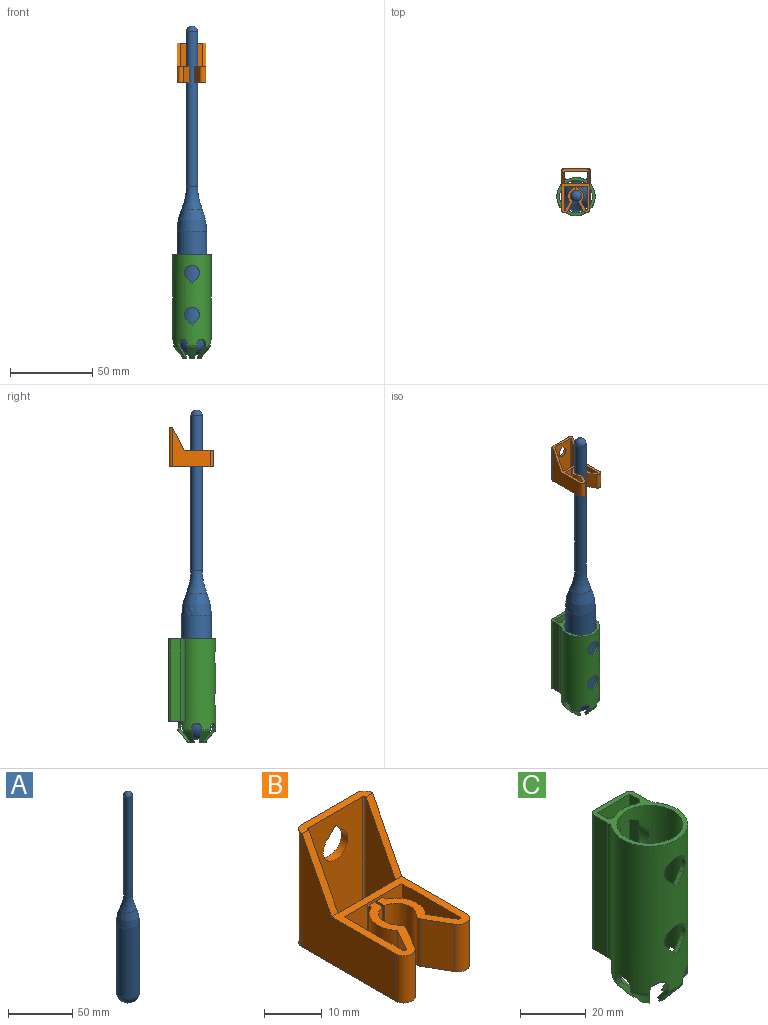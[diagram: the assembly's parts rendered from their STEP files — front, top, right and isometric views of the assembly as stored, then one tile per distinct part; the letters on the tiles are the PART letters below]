
ASSEMBLY  parts=3 mates=2
PART A: 6 faces, bbox 29.1x29.1x200 mm
  f0: cylinder r=9.02mm len=66.27mm, axis (0,0,-1), area 3754.8mm2, adj f1,f5
  f1: revolved ~18.03x18.03mm, area 710.2mm2, adj f0,f2
  f2: torus R=37.97mm, axis (0,0,-1), area 383.7mm2, adj f1,f3
  f3: cylinder r=3.43mm len=94.06mm, axis (0,0,-1), area 2026.6mm2, adj f2,f4
  f4: sphere r=3.43mm, area 73.9mm2, adj f3
  f5: sphere r=9.02mm, area 510.9mm2, adj f0
PART B: 42 faces, bbox 17.2x26.8x24 mm
  f0: plane 24x13.2mm, normal (0,-1,0), area 286.6mm2, adj f5,f7,f13,f27,f39,f40,f41
  f1: plane 24x13.2mm, normal (0,1,0), area 286.6mm2, adj f5,f7,f20,f33,f39,f40,f41
  f2: plane 24x7.2mm, normal (1,0,0), area 122.4mm2, adj f7,f13,f36,f37
  f3: plane 14.03x10mm, normal (-1,0,0), area 140.3mm2, adj f7,f26,f35,f38
  f4: plane 24x22.83mm, normal (1,0,0), area 278.7mm2, adj f7,f32,f33,f34,f35
  f5: plane 17.2x2mm, normal (0,0,1), area 27.2mm2, adj f0,f1,f13,f20,f27,f33,f34,f36
  f6: plane 10x1.6mm, normal (0,1,0), area 16mm2, adj f7,f8,f14,f35
  f7: plane 26.83x17.2mm, normal (0,0,-1), area 186.2mm2, adj f0,f1,f2,f3,f4,f6,f8,f9
  f8: plane 10x0.81mm, normal (-1,0,0), area 8.1mm2, adj f6,f7,f9,f35
  f9: cylinder r=5.03mm len=10mm, axis (0,0,-1), area 95.7mm2, adj f7,f8,f10,f35
  f10: plane 10x4.9mm, normal (-0.87,0.5,0), area 56.6mm2, adj f7,f9,f12,f35
  f11: plane 14.03x10mm, normal (1,0,0), area 140.3mm2, adj f7,f12,f35,f38
  f12: cylinder r=0.4mm len=10mm, axis (0,0,1), area 10.5mm2, adj f7,f10,f11,f35
  f13: cylinder r=0.4mm len=24mm, axis (0,0,1), area 15.1mm2, adj f0,f2,f5,f7
  f14: plane 10x2mm, normal (1,0,0), area 20mm2, adj f6,f7,f15,f35
  f15: cylinder r=3.43mm len=10mm, axis (0,0,-1), area 78.5mm2, adj f7,f14,f16,f35
  f16: cylinder r=1mm len=10mm, axis (0,0,-1), area 13.7mm2, adj f7,f15,f17,f35
  f17: plane 10x5.3mm, normal (0.87,-0.5,0), area 61.2mm2, adj f7,f16,f19,f35
  f18: plane 24x22.83mm, normal (-1,0,0), area 278.7mm2, adj f7,f19,f20,f35,f36
  f19: cylinder r=2mm len=10mm, axis (0,0,1), area 52.4mm2, adj f7,f17,f18,f35
  f20: cylinder r=2mm len=24mm, axis (0,0,1), area 75.4mm2, adj f1,f5,f7,f18
  f21: plane 10x1.6mm, normal (0,1,0), area 16mm2, adj f7,f22,f28,f35
  f22: plane 10x0.81mm, normal (1,0,0), area 8.1mm2, adj f7,f21,f23,f35
  f23: cylinder r=5.03mm len=10mm, axis (0,0,-1), area 95.7mm2, adj f7,f22,f24,f35
  f24: plane 10x4.9mm, normal (0.87,0.5,0), area 56.6mm2, adj f7,f23,f26,f35
  f25: plane 24x7.2mm, normal (-1,0,0), area 122.4mm2, adj f7,f27,f34,f37
  f26: cylinder r=0.4mm len=10mm, axis (0,0,1), area 10.5mm2, adj f3,f7,f24,f35
  f27: cylinder r=0.4mm len=24mm, axis (0,0,1), area 15.1mm2, adj f0,f5,f7,f25
  f28: plane 10x2mm, normal (-1,0,0), area 20mm2, adj f7,f21,f29,f35
  f29: cylinder r=3.43mm len=10mm, axis (0,0,-1), area 78.5mm2, adj f7,f28,f30,f35
  f30: cylinder r=1mm len=10mm, axis (0,0,-1), area 13.7mm2, adj f7,f29,f31,f35
  f31: plane 10x5.3mm, normal (-0.87,-0.5,0), area 61.2mm2, adj f7,f30,f32,f35
  f32: cylinder r=2mm len=10mm, axis (0,0,1), area 52.4mm2, adj f4,f7,f31,f35
  f33: cylinder r=2mm len=24mm, axis (0,0,1), area 75.4mm2, adj f1,f4,f5,f7
  f34: plane 14x7.2mm, normal (0,-0.89,0.46), area 25.2mm2, adj f4,f5,f25,f35
  f35: plane 17.63x17.2mm, normal (0,0,1), area 136mm2, adj f3,f4,f6,f8,f9,f10,f11,f12
  f36: plane 14x7.2mm, normal (0,-0.89,0.46), area 25.2mm2, adj f2,f5,f18,f35
  f37: plane 14x10mm, normal (0,1,0), area 140mm2, adj f2,f7,f25,f35
  f38: plane 14x10mm, normal (0,-1,0), area 140mm2, adj f3,f7,f11,f35
  f39: plane 2.12x2.12mm, normal (-0.71,0,-0.71), area 4.8mm2, adj f0,f1,f40,f41
  f40: plane 2.12x2.12mm, normal (0.71,0,-0.71), area 4.8mm2, adj f0,f1,f39,f41
  f41: cylinder r=3mm len=6mm, axis (0,-1,0), area 22.6mm2, adj f0,f1,f39,f40
PART C: 112 faces, bbox 24.4x29.9x69 mm
  f0: plane 2.52x2.5mm, normal (0,0,-1), area 3.7mm2, adj f9,f14,f62,f87
  f1: plane 2.52x2.5mm, normal (0,0,-1), area 3.7mm2, adj f13,f56,f61,f82
  f2: plane 2.89x2.05mm, normal (0,0,-1), area 3.7mm2, adj f5,f12,f67,f81
  f3: plane 2.52x2.5mm, normal (0,0,-1), area 3.7mm2, adj f6,f11,f65,f72
  f4: plane 2.52x2.5mm, normal (0,0,-1), area 3.7mm2, adj f7,f10,f70,f77
  f5: torus R=11.98mm, axis (0,0,-1), area 0.8mm2, adj f2,f40,f67,f81
  f6: torus R=11.98mm, axis (0,0,-1), area 0.8mm2, adj f3,f39,f65,f72
  f7: torus R=11.98mm, axis (0,0,-1), area 0.8mm2, adj f4,f38,f70,f77
  f8: torus R=11.98mm, axis (0,0,-1), area 0.8mm2, adj f36,f52,f75,f89
  f9: torus R=11.98mm, axis (0,0,-1), area 0.8mm2, adj f0,f55,f62,f87
  f10: torus R=13.51mm, axis (0,0,-1), area 0.4mm2, adj f4,f33,f70,f77
  f11: torus R=13.51mm, axis (0,0,-1), area 0.4mm2, adj f3,f34,f65,f72
  f12: torus R=13.51mm, axis (0,0,-1), area 0.4mm2, adj f2,f35,f67,f81
  f13: torus R=13.51mm, axis (0,0,-1), area 0.4mm2, adj f1,f32,f61,f82
  f14: torus R=13.51mm, axis (0,0,-1), area 0.4mm2, adj f0,f53,f62,f87
  f15: cylinder r=1.6mm len=13.75mm, axis (0,0,1), area 34.5mm2, adj f25,f26,f27,f90,f96
  f16: cylinder r=11.6mm len=15.1mm, axis (0,0,1), area 112.1mm2, adj f26,f29,f30,f103,f104
  f17: cylinder r=1.6mm len=13.75mm, axis (0,0,1), area 34.5mm2, adj f24,f26,f27,f90,f94
  f18: cylinder r=4.5mm len=9mm, axis (0,1,0), area 35.9mm2, adj f19,f20,f27,f28
  f19: plane 3.23x3.23mm, normal (0.71,0,0.71), area 7.3mm2, adj f18,f20,f27,f28
  f20: plane 3.23x3.23mm, normal (-0.71,0,0.71), area 7.3mm2, adj f18,f19,f27,f28
  f21: plane 2.12x2.12mm, normal (0.71,0,0.71), area 4.8mm2, adj f22,f23,f92,f95
  f22: plane 2.12x2.12mm, normal (-0.71,0,0.71), area 4.8mm2, adj f21,f23,f92,f95
  f23: cylinder r=3mm len=6mm, axis (0,-1,0), area 22.6mm2, adj f21,f22,f92,f95
  f24: plane 5.12x5.12mm, normal (0.71,0,0.71), area 11.6mm2, adj f17,f25,f26,f27,f28
  f25: plane 5.12x5.12mm, normal (-0.71,0,0.71), area 11.6mm2, adj f15,f24,f26,f27,f28
  f26: cylinder r=7mm len=14mm, axis (0,-1,0), area 90.2mm2, adj f15,f16,f17,f24,f25,f28,f29,f30
  f27: cylinder r=11.6mm len=54.85mm, axis (0,0,1), area 2691.1mm2, adj f15,f17,f18,f19,f20,f24,f25,f46
  f28: cylinder r=10mm len=54.27mm, axis (0,0,1), area 2821.9mm2, adj f18,f19,f20,f24,f25,f26,f41,f42
  f29: cylinder r=1.6mm len=25.4mm, axis (0,0,1), area 62.3mm2, adj f16,f26,f94,f103,f105
  f30: cylinder r=1.6mm len=25.4mm, axis (0,0,1), area 62.3mm2, adj f16,f26,f96,f104,f105
  f31: cone r=11.23mm half-angle=40deg, axis (0,0,1), area 36mm2, adj f46,f57,f75,f89
  f32: cone r=11.23mm half-angle=40deg, axis (0,0,1), area 36mm2, adj f13,f47,f61,f82
  f33: cone r=11.23mm half-angle=40deg, axis (0,0,1), area 36mm2, adj f10,f48,f70,f77
  f34: cone r=11.23mm half-angle=40deg, axis (0,0,1), area 36mm2, adj f11,f49,f65,f72
  f35: cone r=11.23mm half-angle=40deg, axis (0,0,1), area 36mm2, adj f12,f50,f67,f81
  f36: cone r=10mm half-angle=40deg, axis (0,0,1), area 19.9mm2, adj f8,f41,f75,f76,f88,f89
  f37: cone r=10mm half-angle=40deg, axis (0,0,1), area 19.9mm2, adj f42,f56,f60,f61,f82,f83
  f38: cone r=10mm half-angle=40deg, axis (0,0,1), area 19.9mm2, adj f7,f43,f70,f71,f77,f78
  f39: cone r=10mm half-angle=40deg, axis (0,0,1), area 19.9mm2, adj f6,f44,f65,f66,f72,f73
  f40: cone r=10mm half-angle=40deg, axis (0,0,1), area 19.9mm2, adj f5,f45,f67,f68,f80,f81
  f41: torus R=8mm, axis (0,0,1), area 5.8mm2, adj f28,f36,f76,f88
  f42: torus R=8mm, axis (0,0,1), area 5.8mm2, adj f28,f37,f60,f83
  f43: torus R=8mm, axis (0,0,1), area 5.8mm2, adj f28,f38,f71,f78
  f44: torus R=8mm, axis (0,0,1), area 5.8mm2, adj f28,f39,f66,f73
  f45: torus R=8mm, axis (0,0,1), area 5.8mm2, adj f28,f40,f68,f80
  f46: torus R=9.6mm, axis (0,0,-1), area 8.3mm2, adj f27,f31,f75,f76,f88,f89
  f47: torus R=9.6mm, axis (0,0,-1), area 8.3mm2, adj f27,f32,f60,f61,f82,f83
  f48: torus R=9.6mm, axis (0,0,-1), area 8.3mm2, adj f27,f33,f70,f71,f77,f78
  f49: torus R=9.6mm, axis (0,0,-1), area 8.3mm2, adj f27,f34,f65,f66,f72,f73
  f50: torus R=9.6mm, axis (0,0,-1), area 8.3mm2, adj f27,f35,f67,f68,f80,f81
  f51: plane 28.8x23.2mm, normal (0,0,1), area 161.4mm2, adj f27,f28,f54,f91,f92,f93,f94,f95
  f52: plane 2.89x2.05mm, normal (0,0,-1), area 3.7mm2, adj f8,f57,f75,f89
  f53: cone r=11.23mm half-angle=40deg, axis (0,0,1), area 36mm2, adj f14,f59,f62,f87
  f54: cylinder r=11.6mm len=9.49mm, axis (0,0,1), area 43.5mm2, adj f51,f97,f98,f105
  f55: cone r=10mm half-angle=40deg, axis (0,0,1), area 19.9mm2, adj f9,f58,f62,f63,f86,f87
  f56: torus R=11.98mm, axis (0,0,-1), area 0.8mm2, adj f1,f37,f61,f82
  f57: torus R=13.51mm, axis (0,0,-1), area 0.4mm2, adj f31,f52,f75,f89
  f58: torus R=8mm, axis (0,0,1), area 5.8mm2, adj f28,f55,f63,f86
  f59: torus R=9.6mm, axis (0,0,-1), area 8.3mm2, adj f27,f53,f62,f63,f86,f87
  f60: plane 2.26x1.63mm, normal (0,-1,0), area 2.8mm2, adj f27,f28,f37,f42,f47,f61,f64
  f61: plane 7.68x6.98mm, normal (0,-0.98,0.21), area 15.5mm2, adj f1,f13,f32,f37,f47,f56,f60
  f62: plane 7.68x6.97mm, normal (0,0.98,0.21), area 15.5mm2, adj f0,f9,f14,f53,f55,f59,f63
  f63: plane 2.26x1.63mm, normal (0,1,0), area 2.8mm2, adj f27,f28,f55,f58,f59,f62,f64
  f64: cylinder r=3mm len=6mm, axis (1,0,0), area 15.4mm2, adj f27,f28,f60,f63
  f65: plane 6.98x5.93mm, normal (-0.85,0.49,0.21), area 15.5mm2, adj f3,f6,f11,f34,f39,f49,f66
  f66: plane 1.96x1.63mm, normal (-0.87,0.5,0), area 2.8mm2, adj f27,f28,f39,f44,f49,f65,f69
  f67: plane 7.38x6.97mm, normal (0.85,-0.49,0.21), area 15.5mm2, adj f2,f5,f12,f35,f40,f50,f68
  f68: plane 1.96x1.63mm, normal (0.87,-0.5,0), area 2.8mm2, adj f27,f28,f40,f45,f50,f67,f69
  f69: cylinder r=3mm len=6.23mm, axis (-0.5,-0.87,0), area 15.4mm2, adj f27,f28,f66,f68
  f70: plane 7.68x6.98mm, normal (0,0.98,0.21), area 15.5mm2, adj f4,f7,f10,f33,f38,f48,f71
  f71: plane 2.26x1.63mm, normal (0,1,0), area 2.8mm2, adj f27,f28,f38,f43,f48,f70,f74
  f72: plane 7.68x6.97mm, normal (0,-0.98,0.21), area 15.5mm2, adj f3,f6,f11,f34,f39,f49,f73
  f73: plane 2.26x1.63mm, normal (0,-1,0), area 2.8mm2, adj f27,f28,f39,f44,f49,f72,f74
  f74: cylinder r=3mm len=6mm, axis (-1,0,0), area 15.4mm2, adj f27,f28,f71,f73
  f75: plane 7.38x6.97mm, normal (0.85,0.49,0.21), area 15.5mm2, adj f8,f31,f36,f46,f52,f57,f76
  f76: plane 1.96x1.63mm, normal (0.87,0.5,0), area 2.8mm2, adj f27,f28,f36,f41,f46,f75,f79
  f77: plane 6.98x5.93mm, normal (-0.85,-0.49,0.21), area 15.5mm2, adj f4,f7,f10,f33,f38,f48,f78
  f78: plane 1.96x1.63mm, normal (-0.87,-0.5,0), area 2.8mm2, adj f27,f28,f38,f43,f48,f77,f79
  f79: cylinder r=3mm len=6.23mm, axis (-0.5,0.87,0), area 15.4mm2, adj f27,f28,f76,f78
  f80: plane 1.96x1.63mm, normal (-0.87,-0.5,0), area 2.8mm2, adj f27,f28,f40,f45,f50,f81,f84
  f81: plane 7.38x6.97mm, normal (-0.85,-0.49,0.21), area 15.5mm2, adj f2,f5,f12,f35,f40,f50,f80
  f82: plane 6.98x5.93mm, normal (0.85,0.49,0.21), area 15.5mm2, adj f1,f13,f32,f37,f47,f56,f83
  f83: plane 1.96x1.63mm, normal (0.87,0.5,0), area 2.8mm2, adj f27,f28,f37,f42,f47,f82,f84
  f84: cylinder r=3mm len=6.23mm, axis (0.5,-0.87,0), area 15.4mm2, adj f27,f28,f80,f83
  f85: cylinder r=3mm len=6.23mm, axis (0.5,0.87,0), area 15.4mm2, adj f27,f28,f86,f88
  f86: plane 1.96x1.63mm, normal (0.87,-0.5,0), area 2.8mm2, adj f27,f28,f55,f58,f59,f85,f87
  f87: plane 6.98x5.93mm, normal (0.85,-0.49,0.21), area 15.5mm2, adj f0,f9,f14,f53,f55,f59,f86
  f88: plane 1.96x1.63mm, normal (-0.87,0.5,0), area 2.8mm2, adj f27,f28,f36,f41,f46,f85,f89
  f89: plane 7.38x6.97mm, normal (-0.85,0.49,0.21), area 15.5mm2, adj f8,f31,f36,f46,f52,f57,f88
  f90: plane 19.01x10.55mm, normal (0,0,-1), area 52.8mm2, adj f15,f17,f27,f91,f92,f93,f94,f95
  f91: plane 50x6.08mm, normal (-1,0,0), area 304.1mm2, adj f51,f90,f99,f101
  f92: plane 50x14mm, normal (0,1,0), area 639.6mm2, adj f21,f22,f23,f51,f90,f99,f100,f106
  f93: plane 50x6.08mm, normal (1,0,0), area 304.1mm2, adj f51,f90,f100,f102
  f94: plane 50x3.56mm, normal (1,0,0), area 177.8mm2, adj f17,f29,f51,f90,f95,f97
  f95: plane 50x14mm, normal (0,-1,0), area 639.6mm2, adj f21,f22,f23,f51,f90,f94,f96,f106
  f96: plane 50x3.56mm, normal (-1,0,0), area 177.8mm2, adj f15,f30,f51,f90,f95,f98
  f97: cylinder r=1.6mm len=10.85mm, axis (0,0,1), area 25.3mm2, adj f51,f54,f94,f105
  f98: cylinder r=1.6mm len=10.85mm, axis (0,0,1), area 25.3mm2, adj f51,f54,f96,f105
  f99: cylinder r=1.6mm len=50mm, axis (0,0,-1), area 125.7mm2, adj f51,f90,f91,f92
  f100: cylinder r=1.6mm len=50mm, axis (0,0,-1), area 125.7mm2, adj f51,f90,f92,f93
  f101: cylinder r=5mm len=50mm, axis (0,0,1), area 152.7mm2, adj f27,f51,f90,f91
  f102: cylinder r=5mm len=50mm, axis (0,0,1), area 152.7mm2, adj f27,f51,f90,f93
  f103: plane 5.12x5.12mm, normal (0.71,0,0.71), area 11.6mm2, adj f16,f28,f29,f104,f105
  f104: plane 5.12x5.12mm, normal (-0.71,0,0.71), area 11.6mm2, adj f16,f28,f30,f103,f105
  f105: cylinder r=7mm len=14mm, axis (0,-1,0), area 90.2mm2, adj f28,f29,f30,f54,f97,f98,f103,f104
  f106: plane 2.12x2.12mm, normal (0.71,0,0.71), area 4.8mm2, adj f92,f95,f107,f108
  f107: plane 2.12x2.12mm, normal (-0.71,0,0.71), area 4.8mm2, adj f92,f95,f106,f108
  f108: cylinder r=3mm len=6mm, axis (0,-1,0), area 22.6mm2, adj f92,f95,f106,f107
  f109: cylinder r=4.5mm len=9mm, axis (0,1,0), area 35.9mm2, adj f27,f28,f110,f111
  f110: plane 3.23x3.23mm, normal (0.71,0,0.71), area 7.3mm2, adj f27,f28,f109,f111
  f111: plane 3.23x3.23mm, normal (-0.71,0,0.71), area 7.3mm2, adj f27,f28,f109,f110
PLACE A t=(0,0,1.46)mm
PLACE B t=(-0.25,0,191.13)mm
PLACE C t=(0,0,-4.38)mm
MATE slider B.f9 <-> A.f0  axis (0,0,-1) through (0,0,177.13)mm
MATE slider C.f5 <-> A.f0  axis (0,0,1) through (0,0,62.53)mm
